# Revit family: Plumbing-Fixtures_Accessibility-Professionals-Inc_38-5x37-125-Freedom-ADA-Transfer-Shower
name_source: partatom
category: Plumbing Fixtures
units: mm (PartAtom-declared; Revit-internal decimal feet)

## family parameters
Always vertical = Yes
Cut with Voids When Loaded = No
Enable Cutting in Views = No
Maintain Annotation Orientation = No
OmniClass Number = 23.45.05.14.11.21
OmniClass Title = Shower Receptors
Part Type = Normal
Room Calculation Point = No
Round Connector Dimension = Use Diameter
Shared = No
Work Plane-Based = No

## types (2) — shared parameters
18" x 33 1/2" Grab Bars Height = 35"
24" Grab Bars Height = 40"
Assembly Code = D2010.60
Default Elevation = 0"
Depth = 37"
Description = One-piece ADA transfer shower stall for new construction. Inside dimensions 36" x 36" for ADA compliance, 1″ low threshold, center drain, pre-leveled base, double receiver flange, reinforced wood-backed walls, durable acrylic finish. 30-year warranty, made in the USA. Order with factory-installed folding seat, grab bars, and accessories to meet ADAAG guidelines.
Drain Diameter = 2"
Flow = 0 GPM
Folding Shower Seat Height = 19"
Grab Bars Material = Freedom Showers by Accessibility Professionals Inc. - Steel - Stainless
Grab R = 1/2"
Height = 79"
Horizontal Drain Offset = 19 1/2"
Interior Depth = 36"
Interior Width = 36"
Internal Wall Offset Back = 1 1/2"
Internal Wall Offset Side = 1 1/2"
Keynote = 22 40 00.B5
Manufacturer = Freedom Showers by Accessibility Professionals Inc.
Product Documentation Link = https://www.freedomshowers.com
Product Material = Freedom Showers by Accessibility Professionals Inc. - Fiberglass Acrylic - White
Product Page URL = https://www.freedomshowers.com
Rod Height = 74"
Seat Frame Material = Freedom Showers by Accessibility Professionals Inc. - Steel - Stainless
Seat Material = Freedom Showers by Accessibility Professionals Inc. - Phenolic - White
Shower Valve Height = 41"
Soap Dish Height = 48"
Threshold Height = 1"
URL = https://www.freedomshowers.com
Version = 1
Vertical Drain Offset = 19 1/2"
Water Inlet Diameter = 2"
Width = 38 1/2"

## per-type parameters (varying)
| type | Left | Model | Right |
| 38 ½" x 37 ⅛" Freedom ADA Transfer Shower, Right Valve wall | No | APFQ3838BF1PRRFR | Yes |
| 38 ½" x 37 ⅛" Freedom ADA Transfer Shower, Left Valve Wall | Yes | APFQ3838BF1PRRFL | No |

## geometry (parser evidence)
native form markers: Sweep x13
no freeform markers — native parametric forms only
